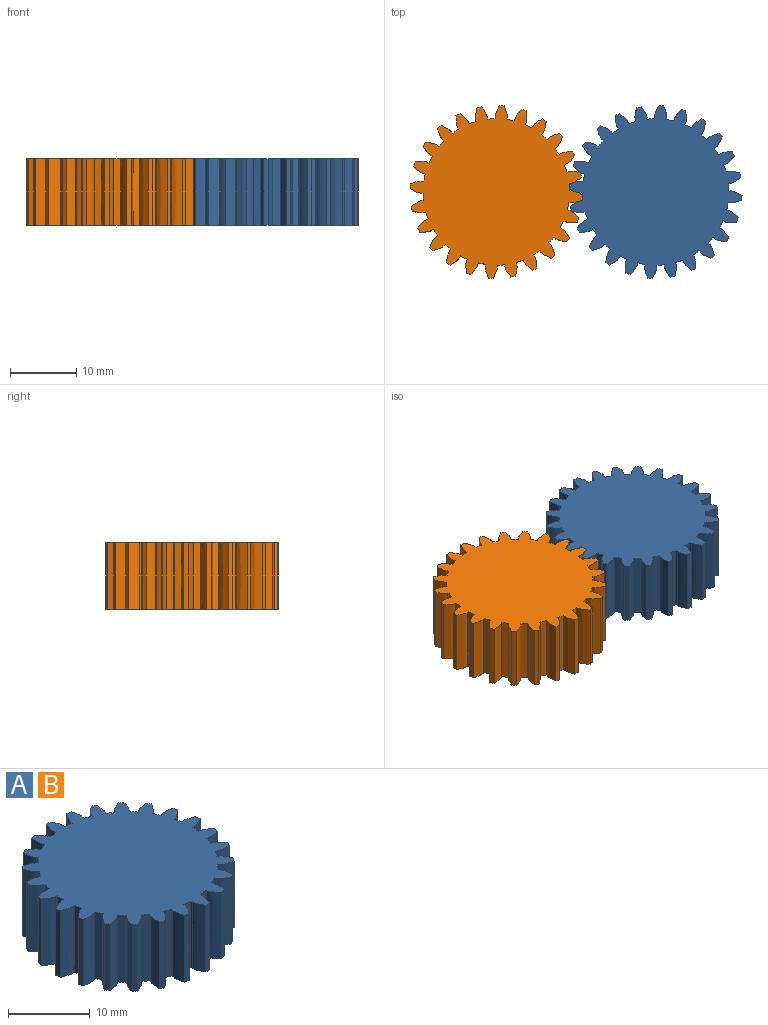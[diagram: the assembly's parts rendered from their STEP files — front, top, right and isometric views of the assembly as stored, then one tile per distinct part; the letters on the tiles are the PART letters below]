
ASSEMBLY  parts=2 mates=1
PART A: 146 faces, bbox 26x26x10 mm
  f0: cylinder r=11.03mm len=10mm, axis (0,0,-1), area 10.7mm2, adj f24,f25,f65,f70
  f1: cylinder r=11.03mm len=10mm, axis (0,0,-1), area 10.7mm2, adj f24,f25,f69,f75
  f2: cylinder r=11.03mm len=10mm, axis (0,0,-1), area 10.7mm2, adj f24,f25,f74,f80
  f3: cylinder r=11.03mm len=10mm, axis (0,0,-1), area 10.7mm2, adj f24,f25,f79,f85
  f4: cylinder r=11.03mm len=10mm, axis (0,0,-1), area 10.7mm2, adj f24,f25,f84,f90
  f5: cylinder r=11.03mm len=10mm, axis (0,0,-1), area 10.7mm2, adj f24,f25,f89,f95
  f6: cylinder r=11.03mm len=10mm, axis (0,0,-1), area 10.7mm2, adj f24,f25,f94,f100
  f7: cylinder r=11.03mm len=10mm, axis (0,0,-1), area 10.7mm2, adj f24,f25,f99,f105
  f8: cylinder r=11.03mm len=10mm, axis (0,0,-1), area 10.7mm2, adj f24,f25,f104,f110
  f9: cylinder r=11.03mm len=10mm, axis (0,0,-1), area 10.7mm2, adj f24,f25,f109,f115
  f10: cylinder r=11.03mm len=10mm, axis (0,0,-1), area 10.7mm2, adj f24,f25,f114,f120
  f11: cylinder r=11.03mm len=10mm, axis (0,0,-1), area 10.7mm2, adj f24,f25,f119,f125
  f12: cylinder r=11.03mm len=10mm, axis (0,0,-1), area 10.7mm2, adj f24,f25,f124,f130
  f13: cylinder r=11.03mm len=10mm, axis (0,0,-1), area 10.7mm2, adj f24,f25,f129,f135
  f14: cylinder r=11.03mm len=10mm, axis (0,0,-1), area 10.7mm2, adj f24,f25,f134,f140
  f15: cylinder r=11.03mm len=10mm, axis (0,0,-1), area 10.7mm2, adj f24,f25,f139,f141
  f16: cylinder r=11.03mm len=10mm, axis (0,0,-1), area 10.7mm2, adj f24,f25,f35,f145
  f17: cylinder r=11.03mm len=10mm, axis (0,0,-1), area 10.7mm2, adj f24,f25,f34,f40
  f18: cylinder r=11.03mm len=10mm, axis (0,0,-1), area 10.7mm2, adj f24,f25,f39,f45
  f19: cylinder r=11.03mm len=10mm, axis (0,0,-1), area 10.7mm2, adj f24,f25,f44,f50
  f20: cylinder r=11.03mm len=10mm, axis (0,0,-1), area 10.7mm2, adj f24,f25,f49,f55
  f21: cylinder r=11.03mm len=10mm, axis (0,0,-1), area 10.7mm2, adj f24,f25,f54,f60
  f22: cylinder r=11.03mm len=10mm, axis (0,0,-1), area 10.7mm2, adj f24,f25,f26,f59
  f23: cylinder r=11.03mm len=10mm, axis (0,0,-1), area 10.7mm2, adj f24,f25,f30,f64
  f24: plane 25.98x25.98mm, normal (0,0,1), area 450.7mm2, adj f0,f1,f2,f3,f4,f5,f6,f7
  f25: plane 25.98x25.98mm, normal (0,0,-1), area 450.7mm2, adj f0,f1,f2,f3,f4,f5,f6,f7
  f26: plane 10x0.25mm, normal (1,0.07,0), area 2.5mm2, adj f22,f24,f25,f27
  f27: extruded ~10x1.72mm, area 18.6mm2, adj f24,f25,f26,f28
  f28: cylinder r=13mm len=10mm, axis (0,0,-1), area 7.1mm2, adj f24,f25,f27,f29
  f29: extruded ~10x1.79mm, area 18.6mm2, adj f24,f25,f28,f30
  f30: plane 10x0.25mm, normal (-1,-0.07,0), area 2.5mm2, adj f23,f24,f25,f29
  f31: extruded ~10x1.72mm, area 18.6mm2, adj f24,f25,f32,f35
  f32: cylinder r=13mm len=10mm, axis (0,0,-1), area 7.1mm2, adj f24,f25,f31,f33
  f33: extruded ~10x1.79mm, area 18.6mm2, adj f24,f25,f32,f34
  f34: plane 10x0.25mm, normal (-0.07,1,0), area 2.5mm2, adj f17,f24,f25,f33
  f35: plane 10x0.25mm, normal (0.07,-1,0), area 2.5mm2, adj f16,f24,f25,f31
  f36: extruded ~10x1.49mm, area 18.6mm2, adj f24,f25,f37,f40
  f37: cylinder r=13mm len=10mm, axis (0,0,-1), area 7.1mm2, adj f24,f25,f36,f38
  f38: extruded ~10x1.84mm, area 18.6mm2, adj f24,f25,f37,f39
  f39: plane 10x0.24mm, normal (-0.32,0.95,0), area 2.5mm2, adj f18,f24,f25,f38
  f40: plane 10x0.24mm, normal (0.32,-0.95,0), area 2.5mm2, adj f17,f24,f25,f36
  f41: extruded ~10x1.43mm, area 18.6mm2, adj f24,f25,f42,f45
  f42: cylinder r=13mm len=10mm, axis (0,0,-1), area 7.1mm2, adj f24,f25,f41,f43
  f43: extruded ~10x1.76mm, area 18.6mm2, adj f24,f25,f42,f44
  f44: plane 10x0.21mm, normal (-0.56,0.83,0), area 2.5mm2, adj f19,f24,f25,f43
  f45: plane 10x0.21mm, normal (0.56,-0.83,0), area 2.5mm2, adj f18,f24,f25,f41
  f46: extruded ~10x1.68mm, area 18.6mm2, adj f24,f25,f47,f50
  f47: cylinder r=13mm len=10mm, axis (0,0,-1), area 7.1mm2, adj f24,f25,f46,f48
  f48: extruded ~10x1.57mm, area 18.6mm2, adj f24,f25,f47,f49
  f49: plane 10x0.19mm, normal (-0.75,0.66,0), area 2.5mm2, adj f20,f24,f25,f48
  f50: plane 10x0.19mm, normal (0.75,-0.66,0), area 2.5mm2, adj f19,f24,f25,f46
  f51: extruded ~10x1.82mm, area 18.6mm2, adj f24,f25,f52,f55
  f52: cylinder r=13mm len=10mm, axis (0,0,-1), area 7.1mm2, adj f24,f25,f51,f53
  f53: extruded ~10x1.33mm, area 18.6mm2, adj f24,f25,f52,f54
  f54: plane 10x0.23mm, normal (-0.9,0.44,0), area 2.5mm2, adj f21,f24,f25,f53
  f55: plane 10x0.23mm, normal (0.9,-0.44,0), area 2.5mm2, adj f20,f24,f25,f51
  f56: extruded ~10x1.83mm, area 18.6mm2, adj f24,f25,f57,f60
  f57: cylinder r=13mm len=10mm, axis (0,0,-1), area 7.1mm2, adj f24,f25,f56,f58
  f58: extruded ~10x1.61mm, area 18.6mm2, adj f24,f25,f57,f59
  f59: plane 10x0.25mm, normal (-0.98,0.2,0), area 2.5mm2, adj f22,f24,f25,f58
  f60: plane 10x0.25mm, normal (0.98,-0.2,0), area 2.5mm2, adj f21,f24,f25,f56
  f61: extruded ~10x1.49mm, area 18.6mm2, adj f24,f25,f62,f64
  f62: cylinder r=13mm len=10mm, axis (0,0,-1), area 7.1mm2, adj f24,f25,f61,f63
  f63: extruded ~10x1.84mm, area 18.6mm2, adj f24,f25,f62,f65
  f64: plane 10x0.24mm, normal (0.95,0.32,0), area 2.5mm2, adj f23,f24,f25,f61
  f65: plane 10x0.24mm, normal (-0.95,-0.32,0), area 2.5mm2, adj f0,f24,f25,f63
  f66: extruded ~10x1.43mm, area 18.6mm2, adj f24,f25,f67,f70
  f67: cylinder r=13mm len=10mm, axis (0,0,-1), area 7.1mm2, adj f24,f25,f66,f68
  f68: extruded ~10x1.76mm, area 18.6mm2, adj f24,f25,f67,f69
  f69: plane 10x0.21mm, normal (-0.83,-0.56,0), area 2.5mm2, adj f1,f24,f25,f68
  f70: plane 10x0.21mm, normal (0.83,0.56,0), area 2.5mm2, adj f0,f24,f25,f66
  f71: extruded ~10x1.68mm, area 18.6mm2, adj f24,f25,f72,f75
  f72: cylinder r=13mm len=10mm, axis (0,0,-1), area 7.1mm2, adj f24,f25,f71,f73
  f73: extruded ~10x1.57mm, area 18.6mm2, adj f24,f25,f72,f74
  f74: plane 10x0.19mm, normal (-0.66,-0.75,0), area 2.5mm2, adj f2,f24,f25,f73
  f75: plane 10x0.19mm, normal (0.66,0.75,0), area 2.5mm2, adj f1,f24,f25,f71
  f76: extruded ~10x1.82mm, area 18.6mm2, adj f24,f25,f77,f80
  f77: cylinder r=13mm len=10mm, axis (0,0,-1), area 7.1mm2, adj f24,f25,f76,f78
  f78: extruded ~10x1.33mm, area 18.6mm2, adj f24,f25,f77,f79
  f79: plane 10x0.23mm, normal (-0.44,-0.9,0), area 2.5mm2, adj f3,f24,f25,f78
  f80: plane 10x0.23mm, normal (0.44,0.9,0), area 2.5mm2, adj f2,f24,f25,f76
  f81: extruded ~10x1.83mm, area 18.6mm2, adj f24,f25,f82,f85
  f82: cylinder r=13mm len=10mm, axis (0,0,-1), area 7.1mm2, adj f24,f25,f81,f83
  f83: extruded ~10x1.61mm, area 18.6mm2, adj f24,f25,f82,f84
  f84: plane 10x0.25mm, normal (-0.2,-0.98,0), area 2.5mm2, adj f4,f24,f25,f83
  f85: plane 10x0.25mm, normal (0.2,0.98,0), area 2.5mm2, adj f3,f24,f25,f81
  f86: extruded ~10x1.72mm, area 18.6mm2, adj f24,f25,f87,f90
  f87: cylinder r=13mm len=10mm, axis (0,0,-1), area 7.1mm2, adj f24,f25,f86,f88
  f88: extruded ~10x1.79mm, area 18.6mm2, adj f24,f25,f87,f89
  f89: plane 10x0.25mm, normal (0.07,-1,0), area 2.5mm2, adj f5,f24,f25,f88
  f90: plane 10x0.25mm, normal (-0.07,1,0), area 2.5mm2, adj f4,f24,f25,f86
  f91: extruded ~10x1.49mm, area 18.6mm2, adj f24,f25,f92,f95
  f92: cylinder r=13mm len=10mm, axis (0,0,-1), area 7.1mm2, adj f24,f25,f91,f93
  f93: extruded ~10x1.84mm, area 18.6mm2, adj f24,f25,f92,f94
  f94: plane 10x0.24mm, normal (0.32,-0.95,0), area 2.5mm2, adj f6,f24,f25,f93
  f95: plane 10x0.24mm, normal (-0.32,0.95,0), area 2.5mm2, adj f5,f24,f25,f91
  f96: extruded ~10x1.43mm, area 18.6mm2, adj f24,f25,f97,f100
  f97: cylinder r=13mm len=10mm, axis (0,0,-1), area 7.1mm2, adj f24,f25,f96,f98
  f98: extruded ~10x1.76mm, area 18.6mm2, adj f24,f25,f97,f99
  f99: plane 10x0.21mm, normal (0.56,-0.83,0), area 2.5mm2, adj f7,f24,f25,f98
  f100: plane 10x0.21mm, normal (-0.56,0.83,0), area 2.5mm2, adj f6,f24,f25,f96
  f101: extruded ~10x1.68mm, area 18.6mm2, adj f24,f25,f102,f105
  f102: cylinder r=13mm len=10mm, axis (0,0,-1), area 7.1mm2, adj f24,f25,f101,f103
  f103: extruded ~10x1.57mm, area 18.6mm2, adj f24,f25,f102,f104
  f104: plane 10x0.19mm, normal (0.75,-0.66,0), area 2.5mm2, adj f8,f24,f25,f103
  f105: plane 10x0.19mm, normal (-0.75,0.66,0), area 2.5mm2, adj f7,f24,f25,f101
  f106: extruded ~10x1.82mm, area 18.6mm2, adj f24,f25,f107,f110
  f107: cylinder r=13mm len=10mm, axis (0,0,-1), area 7.1mm2, adj f24,f25,f106,f108
  f108: extruded ~10x1.33mm, area 18.6mm2, adj f24,f25,f107,f109
  f109: plane 10x0.23mm, normal (0.9,-0.44,0), area 2.5mm2, adj f9,f24,f25,f108
  f110: plane 10x0.23mm, normal (-0.9,0.44,0), area 2.5mm2, adj f8,f24,f25,f106
  f111: extruded ~10x1.83mm, area 18.6mm2, adj f24,f25,f112,f115
  f112: cylinder r=13mm len=10mm, axis (0,0,-1), area 7.1mm2, adj f24,f25,f111,f113
  f113: extruded ~10x1.61mm, area 18.6mm2, adj f24,f25,f112,f114
  f114: plane 10x0.25mm, normal (0.98,-0.2,0), area 2.5mm2, adj f10,f24,f25,f113
  f115: plane 10x0.25mm, normal (-0.98,0.2,0), area 2.5mm2, adj f9,f24,f25,f111
  f116: extruded ~10x1.72mm, area 18.6mm2, adj f24,f25,f117,f120
  f117: cylinder r=13mm len=10mm, axis (0,0,-1), area 7.1mm2, adj f24,f25,f116,f118
  f118: extruded ~10x1.79mm, area 18.6mm2, adj f24,f25,f117,f119
  f119: plane 10x0.25mm, normal (1,0.07,0), area 2.5mm2, adj f11,f24,f25,f118
  f120: plane 10x0.25mm, normal (-1,-0.07,0), area 2.5mm2, adj f10,f24,f25,f116
  f121: extruded ~10x1.49mm, area 18.6mm2, adj f24,f25,f122,f125
  f122: cylinder r=13mm len=10mm, axis (0,0,-1), area 7.1mm2, adj f24,f25,f121,f123
  f123: extruded ~10x1.84mm, area 18.6mm2, adj f24,f25,f122,f124
  f124: plane 10x0.24mm, normal (0.95,0.32,0), area 2.5mm2, adj f12,f24,f25,f123
  f125: plane 10x0.24mm, normal (-0.95,-0.32,0), area 2.5mm2, adj f11,f24,f25,f121
  f126: extruded ~10x1.43mm, area 18.6mm2, adj f24,f25,f127,f130
  f127: cylinder r=13mm len=10mm, axis (0,0,-1), area 7.1mm2, adj f24,f25,f126,f128
  f128: extruded ~10x1.76mm, area 18.6mm2, adj f24,f25,f127,f129
  f129: plane 10x0.21mm, normal (0.83,0.56,0), area 2.5mm2, adj f13,f24,f25,f128
  f130: plane 10x0.21mm, normal (-0.83,-0.56,0), area 2.5mm2, adj f12,f24,f25,f126
  f131: extruded ~10x1.68mm, area 18.6mm2, adj f24,f25,f132,f135
  f132: cylinder r=13mm len=10mm, axis (0,0,-1), area 7.1mm2, adj f24,f25,f131,f133
  f133: extruded ~10x1.57mm, area 18.6mm2, adj f24,f25,f132,f134
  f134: plane 10x0.19mm, normal (0.66,0.75,0), area 2.5mm2, adj f14,f24,f25,f133
  f135: plane 10x0.19mm, normal (-0.66,-0.75,0), area 2.5mm2, adj f13,f24,f25,f131
  f136: extruded ~10x1.82mm, area 18.6mm2, adj f24,f25,f137,f140
  f137: cylinder r=13mm len=10mm, axis (0,0,-1), area 7.1mm2, adj f24,f25,f136,f138
  f138: extruded ~10x1.33mm, area 18.6mm2, adj f24,f25,f137,f139
  f139: plane 10x0.23mm, normal (0.44,0.9,0), area 2.5mm2, adj f15,f24,f25,f138
  f140: plane 10x0.23mm, normal (-0.44,-0.9,0), area 2.5mm2, adj f14,f24,f25,f136
  f141: plane 10x0.25mm, normal (-0.2,-0.98,0), area 2.5mm2, adj f15,f24,f25,f142
  f142: extruded ~10x1.83mm, area 18.6mm2, adj f24,f25,f141,f143
  f143: cylinder r=13mm len=10mm, axis (0,0,-1), area 7.1mm2, adj f24,f25,f142,f144
  f144: extruded ~10x1.61mm, area 18.6mm2, adj f24,f25,f143,f145
  f145: plane 10x0.25mm, normal (0.2,0.98,0), area 2.5mm2, adj f16,f24,f25,f144
PART B: same geometry as A
PLACE A rot(axis=(0,0,-1),52.5deg) t=(34.68,5.72,17.5)mm
PLACE B rot(axis=(1,0,0),180deg) t=(10.68,5.72,27.5)mm fixed
MATE parallel A.f143 <-> B.f32  axis (0,0,1) through (34.68,5.72,27.5)mm
